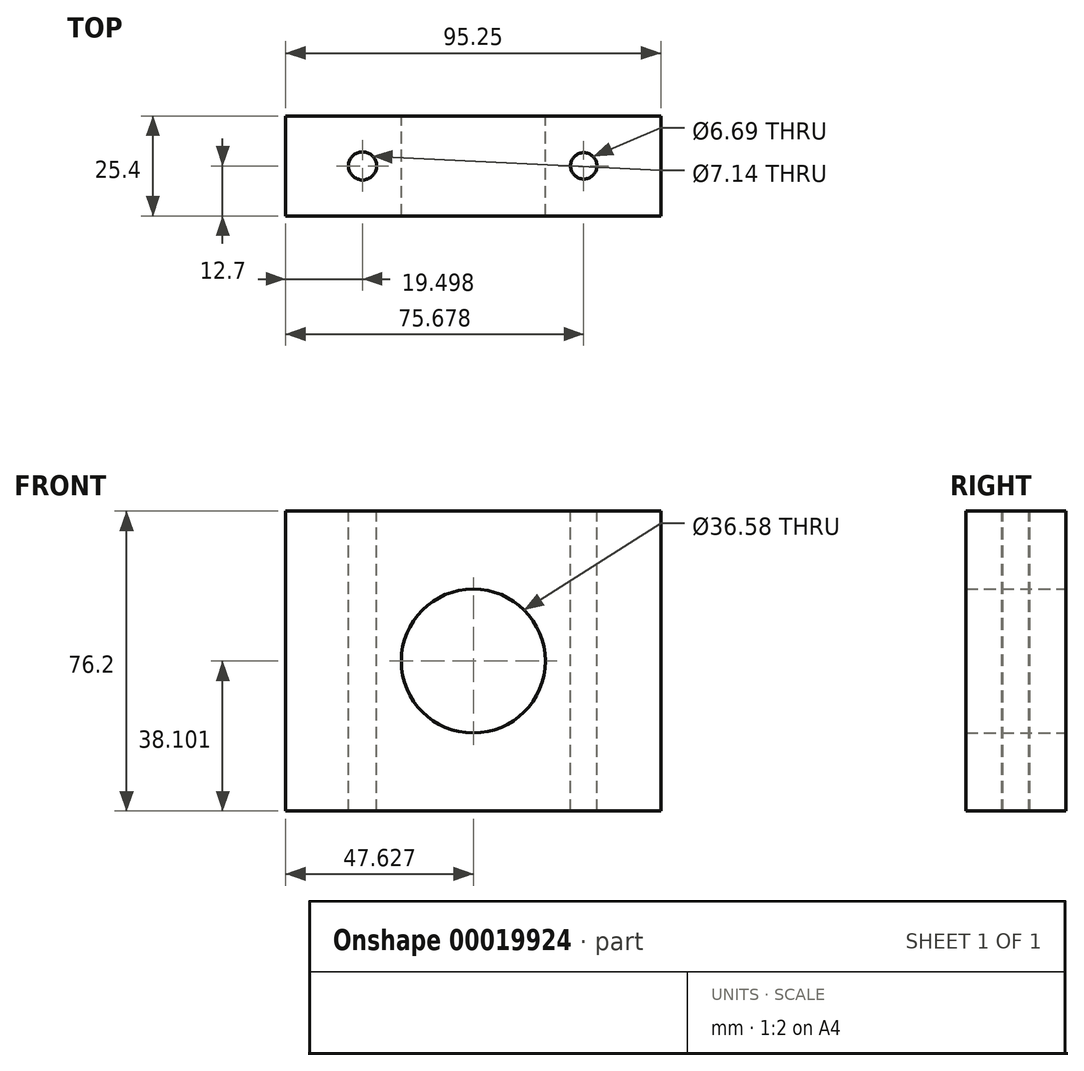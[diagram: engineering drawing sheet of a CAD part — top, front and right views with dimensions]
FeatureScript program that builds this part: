
annotation { "Feature Type Name" : "Feature", "Feature Type Description" : "" }
export const myFeature = defineFeature(function(context is Context, id is Id, definition is map)
    precondition{}
    {
        {
            var Q0;
            Q0=qCreatedBy(makeId("Front.planeOp"),FACE);
            var sketch = newSketch(context, id + "F0", { "sketchPlane" : qUnion([Q0])});
            skLineSegment(sketch, "E0", {"start": v(-40.47, 58.78) * mm, "end": v(-40.47, -17.42) * mm});
            skLineSegment(sketch, "E1", {"start": v(-40.47, -17.42) * mm, "end": v(54.78, -17.42) * mm});
            skLineSegment(sketch, "E2", {"start": v(54.78, -17.42) * mm, "end": v(54.78, 58.78) * mm});
            skLineSegment(sketch, "E3", {"start": v(-40.47, 58.78) * mm, "end": v(54.78, 58.78) * mm});
            skCircle(sketch, "E4", {"center": v(7.16, 20.68) * mm, "radius": 18.29 * mm});
            skLineSegment(sketch, "E5", {"start": v(-11.13, 20.68) * mm, "end": v(-40.47, 20.68) * mm});
            skLineSegment(sketch, "E6", {"start": v(25.45, 20.68) * mm, "end": v(54.78, 20.68) * mm});
            skSolve(sketch);
        }
        {
            var Q0;
            Q0 = qSketchRegion(id + "F0", true);
            extrude(context, id + "F1", {"entities" : qUnion([Q0]), "depth" : 25.4 * mm});
        }
        {
            var Q0;
            Q0=makeQuery(id+"F1.opExtrude","SWEPT_FACE",FACE,{"disambiguationData":[OSD([sQuery(id+"F0.wireOp",EDGE,"E3")])]});
            var sketch = newSketch(context, id + "F2", { "sketchPlane" : qUnion([Q0])});
            skCircle(sketch, "E7", {"center": v(-20.97, -12.7) * mm, "radius": 3.57 * mm});
            skCircle(sketch, "E8", {"center": v(35.2, -12.7) * mm, "radius": 3.35 * mm});
            skSolve(sketch);
        }
        {
            var Q0;
            Q0=makeQuery(id+"F2.imprint","IMPRINT",FACE,{"disambiguationData":[TD([[makeQuery(id+"F2.imprint","IMPRINT",EDGE,{"derivedFrom":sQuery(id+"F2.wireOp",EDGE,"E7")}),1.0]])]});
            var Q1;
            Q1=makeQuery(id+"F2.imprint","IMPRINT",FACE,{"disambiguationData":[TD([[makeQuery(id+"F2.imprint","IMPRINT",EDGE,{"derivedFrom":sQuery(id+"F2.wireOp",EDGE,"E8")}),1.0]])]});
            extrude(context, id + "F3", {"entities" : qUnion([Q0, Q1]), "operationType" : NewBodyOperationType.REMOVE, "endBound" : BoundingType.THROUGH_ALL, "oppositeDirection" : true, "depth" : 76.2 * mm});
        }
    });
